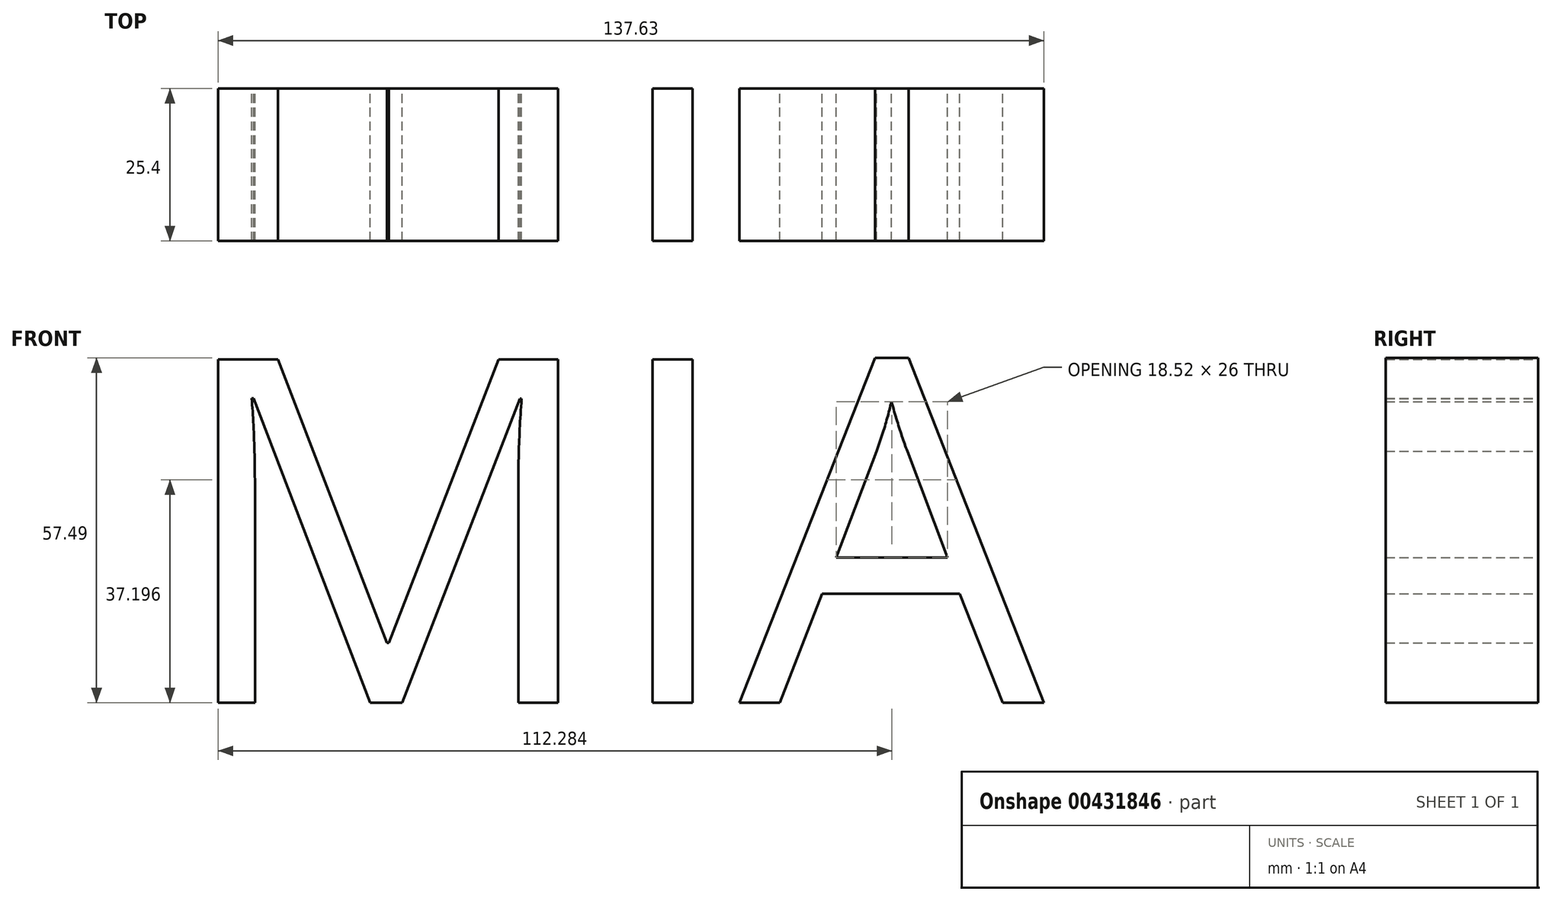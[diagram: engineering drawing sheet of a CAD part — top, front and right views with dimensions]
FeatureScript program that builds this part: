
annotation { "Feature Type Name" : "Feature", "Feature Type Description" : "" }
export const myFeature = defineFeature(function(context is Context, id is Id, definition is map)
    precondition{}
    {
        {
            var Q0;
            Q0=qCreatedBy(makeId("Front.planeOp"),FACE);
            var sketch = newSketch(context, id + "F0", { "sketchPlane" : qUnion([Q0])});
            skText(sketch, "E0", { "text": "MIA\n", "fontName": "OpenSans-Regular.ttf"});
            const initialGuessF0  = {"E0": [-0.02783, 0, 1, 0, 0.05774]};
            skSetInitialGuess(sketch, initialGuessF0);
            skSolve(sketch);
        }
        {
            var Q0;
            Q0=makeQuery(id+"F0.imprint","IMPRINT",FACE,{"disambiguationData":[TD([[makeQuery(id+"F0.imprint","IMPRINT",EDGE,{"derivedFrom":sQuery(id+"F0.wireOp",EDGE,"E0.sketch_text.stroke-0")}),-1.0]])]});
            var Q1;
            Q1=makeQuery(id+"F0.imprint","IMPRINT",FACE,{"disambiguationData":[TD([[makeQuery(id+"F0.imprint","IMPRINT",EDGE,{"derivedFrom":sQuery(id+"F0.wireOp",EDGE,"E0.sketch_text.stroke-18")}),-1.0]])]});
            var Q2;
            Q2=makeQuery(id+"F0.imprint","IMPRINT",FACE,{"disambiguationData":[TD([[makeQuery(id+"F0.imprint","IMPRINT",EDGE,{"derivedFrom":sQuery(id+"F0.wireOp",EDGE,"E0.sketch_text.stroke-22")}),-1.0]])]});
            extrude(context, id + "F1", {"entities" : qUnion([Q0, Q1, Q2]), "endBound" : BoundingType.SYMMETRIC, "depth" : 25.4 * mm});
        }
    });
